# Revit family: QMXD-HP_Horizontal
name_source: partatom
category: Mechanical Equipment
units: mm (PartAtom-declared; Revit-internal decimal feet)

## family parameters
Always vertical = Yes
Cut with Voids When Loaded = No
OmniClass Number = 23.75.35.17
OmniClass Title = Fans
Part Type = Normal
Room Calculation Point = No
Round Connector Dimension = Use Radius
Shared = No
Work Plane-Based = No

## types (18) — shared parameters
0 = 0"
1.5 = 1 1/2"
1.9375 = 1 15/16"
3 = 3"
45 = 45.00°
90 = 90.00°
Manufacturer = Loren Cook Company
Model = QMX
ONE EIGTH = 1/8"
ROTATION = 45.00°
Type Comments = Mixed Flow Inline Horizontal Mount Belt Drive Arrangement 9
URL = www.lorencook.com

## per-type parameters (varying)
- 90-QMX-HP_HOR: (A/2)-.125=6 9/32"; (F+3)/2=7 11/16"; (G/2)-.75=8 7/16"; -(B/2)=-9 15/16"; -(G/2)-.75=-8 7/16"; -B/3*2=-13 1/4"; A=12 13/16"; A/2=6 13/32"; A/4=3 7/32"; A/8=1 19/32"; B=19 7/8"; B/10=2"; B/2=9 15/16"; B/3*2=13 1/4"; B/6=3 5/16"; B/8=3 5/16"; C=15 7/8"; C/2=7 15/16"; D=8 1/2"; E=31 1/4"; E-D=22 3/4"; E-D-1.5=21 1/4"; F=12 3/8"; F+1.5=13 7/8"; F-1.5=10 7/8"; F/2=6 3/16"; G=18 3/8"; G+1.5=19 7/8"; G/2=9 3/16"; H=1/2"; H/2=1/4"; MCHALF=6"; MOTORCOVER=12"
- 120-QMX-HP_HOR: (A/2)-.125=8 13/32"; (F+3)/2=9 1/4"; (G/2)-.75=10 1/2"; -(B/2)=-12"; -(G/2)-.75=-10 1/2"; -B/3*2=-16"; A=17 1/16"; A/2=8 17/32"; A/4=4 9/32"; A/8=2 1/8"; B=24"; B/10=2 13/32"; B/2=12"; B/3*2=16"; B/6=4"; B/8=4"; C=20 1/16"; C/2=10 1/32"; D=10 1/2"; E=36 11/16"; E-D=26 3/16"; E-D-1.5=24 11/16"; F=15 1/2"; F+1.5=17"; F-1.5=14"; F/2=7 3/4"; G=22 1/2"; G+1.5=24"; G/2=11 1/4"; H=1/2"; H/2=1/4"; MCHALF=8"; MOTORCOVER=16"
- 135-QMX-HP_HOR: (A/2)-.125=9 1/2"; (F+3)/2=10 1/4"; (G/2)-.75=12"; -(B/2)=-13 1/2"; -(G/2)-.75=-12"; -B/3*2=-18"; A=19 1/4"; A/2=9 5/8"; A/4=4 13/16"; A/8=2 13/32"; B=27"; B/10=2 11/16"; B/2=13 1/2"; B/3*2=18"; B/6=4 1/2"; B/8=4 1/2"; C=22 1/4"; C/2=11 1/8"; D=12"; E=39 1/2"; E-D=27 1/2"; E-D-1.5=26"; F=17 1/2"; F+1.5=19"; F-1.5=16"; F/2=8 3/4"; G=25 1/2"; G+1.5=27"; G/2=12 3/4"; H=1/2"; H/2=1/4"; MCHALF=9"; MOTORCOVER=18"
- 150-QMX-HP_HOR: (A/2)-.125=10 9/16"; (F+3)/2=10 7/8"; (G/2)-.75=13 9/16"; -(B/2)=-15"; -(G/2)-.75=-13 9/16"; -B/3*2=-20"; A=21 3/8"; A/2=10 11/16"; A/4=5 11/32"; A/8=2 11/16"; B=30"; B/10=3"; B/2=15"; B/3*2=20"; B/6=5"; B/8=5"; C=24 3/8"; C/2=12 3/16"; D=13 3/16"; E=42 1/16"; E-D=28 7/8"; E-D-1.5=27 3/8"; F=18 3/4"; F+1.5=20 1/4"; F-1.5=17 1/4"; F/2=9 3/8"; G=28 5/8"; G+1.5=30 1/8"; G/2=14 5/16"; H=1/2"; H/2=1/4"; MCHALF=10"; MOTORCOVER=20"
- 165-QMX-HP_HOR: (A/2)-.125=11 5/8"; (F+3)/2=11 29/32"; (G/2)-.75=15 1/16"; -(B/2)=-16 1/2"; -(G/2)-.75=-15 1/16"; -B/3*2=-22"; A=23 1/2"; A/2=11 3/4"; A/4=5 7/8"; A/8=2 15/16"; B=33"; B/10=3 5/16"; B/2=16 1/2"; B/3*2=22"; B/6=5 1/2"; B/8=5 1/2"; C=26 1/2"; C/2=13 1/4"; D=14 5/16"; E=43 3/4"; E-D=29 7/16"; E-D-1.5=27 15/16"; F=20 13/16"; F+1.5=22 5/16"; F-1.5=19 5/16"; F/2=10 13/32"; G=31 5/8"; G+1.5=33 1/8"; G/2=15 13/16"; H=1/2"; H/2=1/4"; MCHALF=10"; MOTORCOVER=20"
- 180-QMX-HP_HOR: (A/2)-.125=12 11/16"; (F+3)/2=12 29/32"; (G/2)-.75=16 1/16"; -(B/2)=-17 1/2"; -(G/2)-.75=-16 1/16"; -B/3*2=-23 11/32"; A=25 5/8"; A/2=12 13/16"; A/4=6 13/32"; A/8=3 7/32"; B=35"; B/10=3 1/2"; B/2=17 1/2"; B/3*2=23 11/32"; B/6=5 27/32"; B/8=5 27/32"; C=28 5/8"; C/2=14 5/16"; D=15 1/2"; E=46 1/4"; E-D=30 3/4"; E-D-1.5=29 1/4"; F=22 13/16"; F+1.5=24 5/16"; F-1.5=21 5/16"; F/2=11 13/32"; G=33 5/8"; G+1.5=35 1/8"; G/2=16 13/16"; H=9/16"; H/2=9/32"; MCHALF=10"; MOTORCOVER=20"
- 202-QMX-HP_HOR: (A/2)-.125=14 1/4"; (F+3)/2=13 5/8"; (G/2)-.75=17 5/16"; -(B/2)=-18 3/4"; -(G/2)-.75=-17 5/16"; -B/3*2=-25"; A=28 3/4"; A/2=14 3/8"; A/4=7 3/16"; A/8=3 19/32"; B=37 1/2"; B/10=3 3/4"; B/2=18 3/4"; B/3*2=25"; B/6=6 1/4"; B/8=6 1/4"; C=31 3/4"; C/2=15 7/8"; D=17 1/4"; E=49 15/16"; E-D=32 11/16"; E-D-1.5=31 3/16"; F=24 1/4"; F+1.5=25 3/4"; F-1.5=22 3/4"; F/2=12 1/8"; G=36 1/8"; G+1.5=37 5/8"; G/2=18 1/16"; H=9/16"; H/2=9/32"; MCHALF=10"; MOTORCOVER=20"
- 225-QMX-HP_HOR: (A/2)-.125=15 27/32"; (F+3)/2=14 31/32"; (G/2)-.75=19 1/16"; -(B/2)=-20 1/2"; -(G/2)-.75=-19 1/16"; -B/3*2=-27 11/32"; A=31 15/16"; A/2=15 31/32"; A/4=8"; A/8=4"; B=41"; B/10=4 3/32"; B/2=20 1/2"; B/3*2=27 11/32"; B/6=6 27/32"; B/8=6 27/32"; C=34 15/16"; C/2=17 15/32"; D=19"; E=55 13/16"; E-D=36 13/16"; E-D-1.5=35 5/16"; F=26 15/16"; F+1.5=28 7/16"; F-1.5=25 7/16"; F/2=13 15/32"; G=39 5/8"; G+1.5=41 1/8"; G/2=19 13/16"; H=9/16"; H/2=9/32"; MCHALF=10 21/32"; MOTORCOVER=21 9/32"
- 245-QMX-HP_HOR: (A/2)-.125=17 1/4"; (F+3)/2=15 31/32"; (G/2)-.75=20 13/16"; -(B/2)=-22 1/4"; -(G/2)-.75=-20 13/16"; -B/3*2=-29 21/32"; A=34 3/4"; A/2=17 3/8"; A/4=8 11/16"; A/8=4 11/32"; B=44 1/2"; B/10=4 7/16"; B/2=22 1/4"; B/3*2=29 21/32"; B/6=7 13/32"; B/8=7 13/32"; C=37 3/4"; C/2=18 7/8"; D=20 1/2"; E=59"; E-D=38 1/2"; E-D-1.5=37"; F=28 15/16"; F+1.5=30 7/16"; F-1.5=27 7/16"; F/2=14 15/32"; G=43 1/8"; G+1.5=44 5/8"; G/2=21 9/16"; H=11/16"; H/2=11/32"; MCHALF=11 19/32"; MOTORCOVER=23 5/32"
- 270-QMX-HP_HOR: (A/2)-.125=19 1/32"; (F+3)/2=17"; (G/2)-.75=22 1/16"; -(B/2)=-23 1/2"; -(G/2)-.75=-22 1/16"; -B/3*2=-31 11/32"; A=38 5/16"; A/2=19 5/32"; A/4=9 19/32"; A/8=4 25/32"; B=47"; B/10=4 11/16"; B/2=23 1/2"; B/3*2=31 11/32"; B/6=7 27/32"; B/8=7 27/32"; C=41 5/16"; C/2=20 21/32"; D=22 7/16"; E=62 7/8"; E-D=40 7/16"; E-D-1.5=38 15/16"; F=31"; F+1.5=32 1/2"; F-1.5=29 1/2"; F/2=15 1/2"; G=45 5/8"; G+1.5=47 1/8"; G/2=22 13/16"; H=11/16"; H/2=11/32"; MCHALF=12 25/32"; MOTORCOVER=25 17/32"
- 300-QMX-HP_HOR: (A/2)-.125=21 1/8"; (F+3)/2=18 3/8"; (G/2)-.75=25 9/16"; -(B/2)=-27"; -(G/2)-.75=-25 9/16"; -B/3*2=-36"; A=42 1/2"; A/2=21 1/4"; A/4=10 5/8"; A/8=5 5/16"; B=54"; B/10=5 13/32"; B/2=27"; B/3*2=36"; B/6=9"; B/8=9"; C=45 1/2"; C/2=22 3/4"; D=24 3/4"; E=68 1/16"; E-D=43 5/16"; E-D-1.5=41 13/16"; F=33 3/4"; F+1.5=35 1/4"; F-1.5=32 1/4"; F/2=16 7/8"; G=52 5/8"; G+1.5=54 1/8"; G/2=26 5/16"; H=11/16"; H/2=11/32"; MCHALF=14 5/32"; MOTORCOVER=28 11/32"
- 330-QMX-HP_HOR: (A/2)-.125=23 1/4"; (F+3)/2=19 7/8"; (G/2)-.75=27 13/16"; -(B/2)=-29 1/4"; -(G/2)-.75=-27 13/16"; -B/3*2=-39"; A=46 3/4"; A/2=23 3/8"; A/4=11 11/16"; A/8=5 27/32"; B=58 1/2"; B/10=5 27/32"; B/2=29 1/4"; B/3*2=39"; B/6=9 3/4"; B/8=9 3/4"; C=49 3/4"; C/2=24 7/8"; D=27"; E=74 13/16"; E-D=47 13/16"; E-D-1.5=46 5/16"; F=36 3/4"; F+1.5=38 1/4"; F-1.5=35 1/4"; F/2=18 3/8"; G=57 1/8"; G+1.5=58 5/8"; G/2=28 9/16"; H=11/16"; H/2=11/32"; MCHALF=15 19/32"; MOTORCOVER=31 5/32"
- 365-QMX-HP_HOR: (A/2)-.125=25 3/4"; (F+3)/2=21 3/4"; (G/2)-.75=30 15/16"; -(B/2)=-32"; -(G/2)-.75=-30 15/16"; -B/3*2=-42 21/32"; A=51 3/4"; A/2=25 7/8"; A/4=12 15/16"; A/8=6 15/32"; B=64"; B/10=6 13/32"; B/2=32"; B/3*2=42 21/32"; B/6=10 21/32"; B/8=10 21/32"; C=54 3/4"; C/2=27 3/8"; D=29 13/16"; E=80 1/4"; E-D=50 7/16"; E-D-1.5=48 15/16"; F=40 1/2"; F+1.5=42"; F-1.5=39"; F/2=20 1/4"; G=63 3/8"; G+1.5=64 7/8"; G/2=31 11/16"; H=13/16"; H/2=13/32"; MCHALF=17 1/4"; MOTORCOVER=34 1/2"
- 402-QMX-HP_HOR: (A/2)-.125=28 11/32"; (F+3)/2=23 1/2"; (G/2)-.75=33 3/16"; -(B/2)=-34 1/4"; -(G/2)-.75=-33 3/16"; -B/3*2=-45 21/32"; A=56 15/16"; A/2=28 15/32"; A/4=14 1/4"; A/8=7 1/8"; B=68 1/2"; B/10=6 27/32"; B/2=34 1/4"; B/3*2=45 21/32"; B/6=11 13/32"; B/8=11 13/32"; C=59 15/16"; C/2=29 31/32"; D=32 11/16"; E=88 5/16"; E-D=55 5/8"; E-D-1.5=54 1/8"; F=44"; F+1.5=45 1/2"; F-1.5=42 1/2"; F/2=22"; G=67 7/8"; G+1.5=69 3/8"; G/2=33 15/16"; H=13/16"; H/2=13/32"; MCHALF=18 31/32"; MOTORCOVER=37 31/32"
- 445-QMX-HP_HOR: (A/2)-.125=31 13/32"; (F+3)/2=25 5/8"; (G/2)-.75=35 15/16"; -(B/2)=-37"; -(G/2)-.75=-35 15/16"; -B/3*2=-49 11/32"; A=63 1/16"; A/2=31 17/32"; A/4=15 25/32"; A/8=7 7/8"; B=74"; B/10=7 13/32"; B/2=37"; B/3*2=49 11/32"; B/6=12 11/32"; B/8=12 11/32"; C=66 1/16"; C/2=33 1/32"; D=36"; E=94 7/8"; E-D=58 7/8"; E-D-1.5=57 3/8"; F=48 1/4"; F+1.5=49 3/4"; F-1.5=46 3/4"; F/2=24 1/8"; G=73 3/8"; G+1.5=74 7/8"; G/2=36 11/16"; H=13/16"; H/2=13/32"; MCHALF=21 1/32"; MOTORCOVER=42 1/32"
- 490-QMX-HP_HOR: (A/2)-.125=34 9/16"; (F+3)/2=27 7/8"; (G/2)-.75=39 3/16"; -(B/2)=-40 1/4"; -(G/2)-.75=-39 3/16"; -B/3*2=-53 21/32"; A=69 3/8"; A/2=34 11/16"; A/4=17 11/32"; A/8=8 11/16"; B=80 1/2"; B/10=8 1/16"; B/2=40 1/4"; B/3*2=53 21/32"; B/6=13 13/32"; B/8=13 13/32"; C=72 3/8"; C/2=36 3/16"; D=39 7/16"; E=103 3/8"; E-D=63 15/16"; E-D-1.5=62 7/16"; F=52 3/4"; F+1.5=54 1/4"; F-1.5=51 1/4"; F/2=26 3/8"; G=79 7/8"; G+1.5=81 3/8"; G/2=39 15/16"; H=13/16"; H/2=13/32"; MCHALF=23 1/8"; MOTORCOVER=46 1/4"
- 540-QMX-HP_HOR: (A/2)-.125=38 3/32"; (F+3)/2=30 1/2"; (G/2)-.75=42 7/16"; -(B/2)=-43 1/2"; -(G/2)-.75=-42 7/16"; -B/3*2=-58"; A=76 7/16"; A/2=38 7/32"; A/4=19 1/8"; A/8=9 9/16"; B=87"; B/10=8 11/16"; B/2=43 1/2"; B/3*2=58"; B/6=14 1/2"; B/8=14 1/2"; C=79 7/16"; C/2=39 23/32"; D=43 5/16"; E=110 15/16"; E-D=67 5/8"; E-D-1.5=66 1/8"; F=58"; F+1.5=59 1/2"; F-1.5=56 1/2"; F/2=29"; G=86 3/8"; G+1.5=87 7/8"; G/2=43 3/16"; H=13/16"; H/2=13/32"; MCHALF=25 15/32"; MOTORCOVER=50 31/32"
- 600-QMX-HP_HOR: (A/2)-.125=42 5/16"; (F+3)/2=33 1/2"; (G/2)-.75=46 11/16"; -(B/2)=-47 3/4"; -(G/2)-.75=-46 11/16"; -B/3*2=-63 21/32"; A=84 7/8"; A/2=42 7/16"; A/4=21 7/32"; A/8=10 5/8"; B=95 1/2"; B/10=9 9/16"; B/2=47 3/4"; B/3*2=63 21/32"; B/6=15 29/32"; B/8=15 29/32"; C=87 7/8"; C/2=43 15/16"; D=50"; E=122 1/16"; E-D=72 1/16"; E-D-1.5=70 9/16"; F=64"; F+1.5=65 1/2"; F-1.5=62 1/2"; F/2=32"; G=94 7/8"; G+1.5=96 3/8"; G/2=47 7/16"; H=13/16"; H/2=13/32"; MCHALF=25 15/32"; MOTORCOVER=50 31/32"

## geometry (parser evidence)
native form markers: Sweep x2
no freeform markers — native parametric forms only
